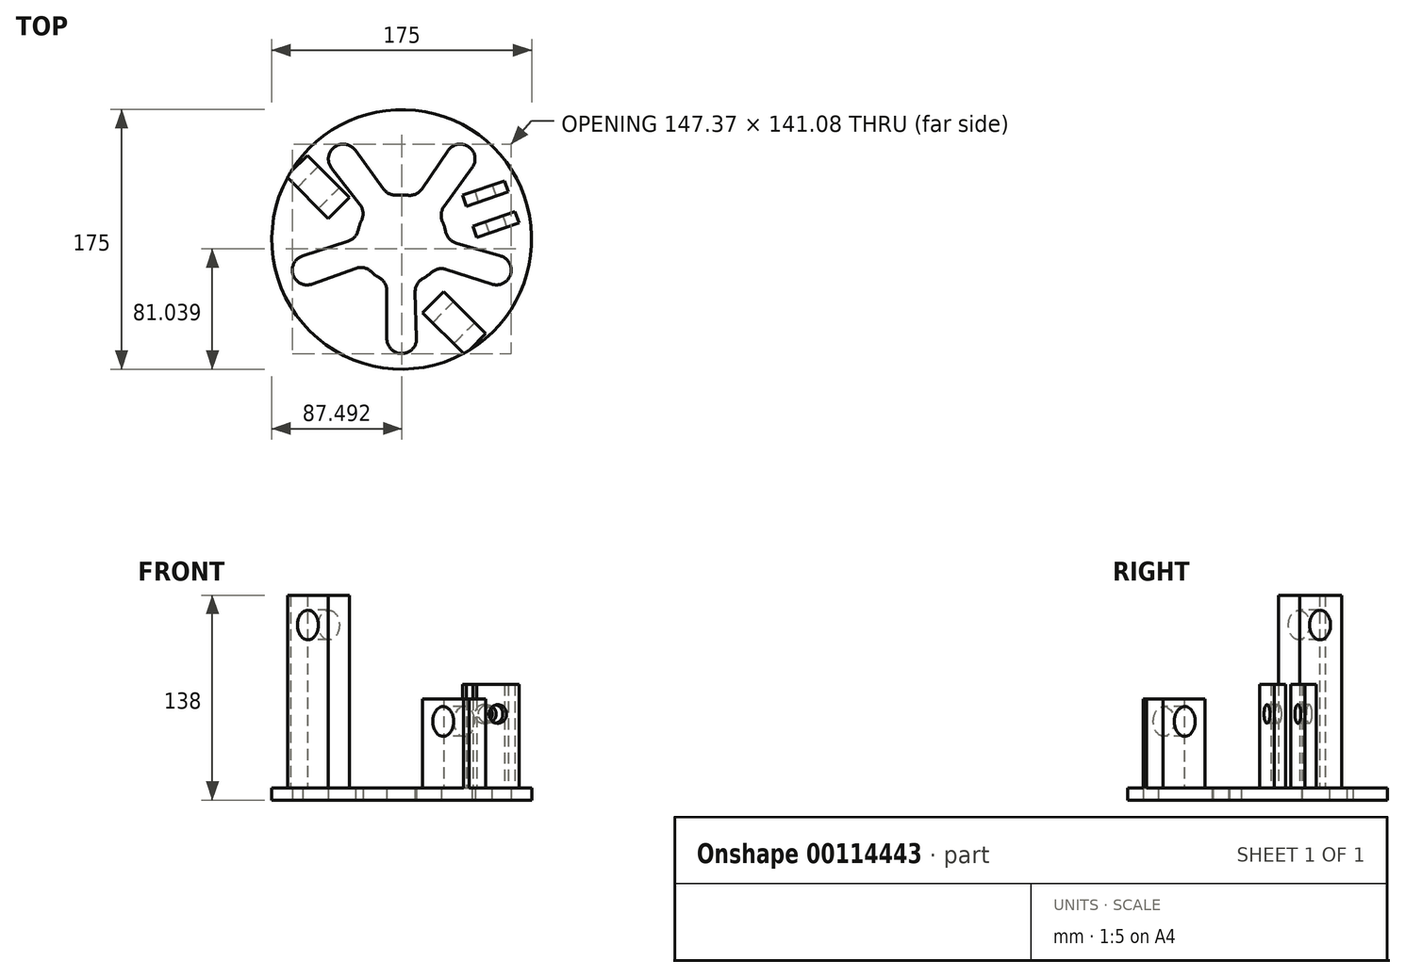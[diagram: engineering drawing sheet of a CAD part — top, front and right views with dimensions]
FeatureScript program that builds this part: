
annotation { "Feature Type Name" : "Feature", "Feature Type Description" : "" }
export const myFeature = defineFeature(function(context is Context, id is Id, definition is map)
    precondition{}
    {
        {
            var Q0;
            Q0=qCreatedBy(makeId("Top.planeOp"),FACE);
            var sketch = newSketch(context, id + "F0", { "sketchPlane" : qUnion([Q0])});
            skCircle(sketch, "E0", {"center": v(0, 0) * mm, "radius": 87.5 * mm});
            skPoint(sketch, "E1.2.0", {"position": v(8.8, -28.68) * mm});
            skLineSegment(sketch, "E1.2.1", {"start": v(-10, -66.87) * mm, "end": v(-10, -34.64) * mm});
            skLineSegment(sketch, "E1.2.2", {"start": v(10, -66.69) * mm, "end": v(9.02, -35.5) * mm});
            skArc(sketch, "E1.2.3", {"start": v(-10, -66.87) * mm, "mid": v(0.1, -77) * mm, "end": v(10, -66.69) * mm});
            skPoint(sketch, "E1.2.4", {"position": v(-10, -28.28) * mm});
            skArc(sketch, "E1.2.5", {"start": v(-10, -34.64) * mm, "mid": v(-11.34, -29.64) * mm, "end": v(-15, -25.98) * mm});
            skArc(sketch, "E1.2.6", {"start": v(14.26, -26.4) * mm, "mid": v(10.35, -30.2) * mm, "end": v(9.02, -35.5) * mm});
            skPoint(sketch, "E2.1.0", {"position": v(30, -0.49) * mm});
            skLineSegment(sketch, "E2.1.1", {"start": v(60.51, -30.17) * mm, "end": v(29.86, -20.21) * mm});
            skLineSegment(sketch, "E2.1.2", {"start": v(66.51, -11.1) * mm, "end": v(36.55, -2.4) * mm});
            skPoint(sketch, "E2.1.3", {"position": v(23.81, -18.25) * mm});
            skArc(sketch, "E2.1.4", {"start": v(60.51, -30.17) * mm, "mid": v(73.26, -23.7) * mm, "end": v(66.51, -11.1) * mm});
            skArc(sketch, "E2.1.5", {"start": v(29.86, -20.21) * mm, "mid": v(24.69, -19.94) * mm, "end": v(20.07, -22.3) * mm});
            skArc(sketch, "E2.1.6", {"start": v(29.5, 5.4) * mm, "mid": v(31.92, 0.5) * mm, "end": v(36.55, -2.4) * mm});
            skPoint(sketch, "E2.2.0", {"position": v(9.73, 28.38) * mm});
            skLineSegment(sketch, "E2.2.1", {"start": v(47.4, 48.22) * mm, "end": v(28.45, 22.15) * mm});
            skLineSegment(sketch, "E2.2.2", {"start": v(31.11, 59.83) * mm, "end": v(13.57, 34.03) * mm});
            skPoint(sketch, "E2.2.3", {"position": v(24.71, 17) * mm});
            skArc(sketch, "E2.2.4", {"start": v(47.4, 48.22) * mm, "mid": v(45.18, 62.35) * mm, "end": v(31.11, 59.83) * mm});
            skArc(sketch, "E2.2.5", {"start": v(28.45, 22.15) * mm, "mid": v(26.6, 17.32) * mm, "end": v(27.4, 12.2) * mm});
            skArc(sketch, "E2.2.6", {"start": v(3.98, 29.74) * mm, "mid": v(9.38, 30.52) * mm, "end": v(13.57, 34.03) * mm});
            skPoint(sketch, "E2.3.0", {"position": v(-23.98, 18.03) * mm});
            skLineSegment(sketch, "E2.3.1", {"start": v(-31.22, 59.98) * mm, "end": v(-12.27, 33.9) * mm});
            skLineSegment(sketch, "E2.3.2", {"start": v(-47.28, 48.08) * mm, "end": v(-28.17, 23.42) * mm});
            skPoint(sketch, "E2.3.3", {"position": v(-8.54, 28.76) * mm});
            skArc(sketch, "E2.3.4", {"start": v(-31.22, 59.98) * mm, "mid": v(-45.33, 62.24) * mm, "end": v(-47.28, 48.08) * mm});
            skArc(sketch, "E2.3.5", {"start": v(-12.27, 33.9) * mm, "mid": v(-8.25, 30.65) * mm, "end": v(-3.14, 29.84) * mm});
            skArc(sketch, "E2.3.6", {"start": v(-27.05, 12.97) * mm, "mid": v(-26.12, 18.36) * mm, "end": v(-28.17, 23.42) * mm});
            skPoint(sketch, "E2.4.0", {"position": v(-24.55, -17.24) * mm});
            skLineSegment(sketch, "E2.4.1", {"start": v(-66.69, -11.16) * mm, "end": v(-36.04, -1.2) * mm});
            skLineSegment(sketch, "E2.4.2", {"start": v(-60.33, -30.11) * mm, "end": v(-30.98, -19.55) * mm});
            skPoint(sketch, "E2.4.3", {"position": v(-30, 0.77) * mm});
            skArc(sketch, "E2.4.4", {"start": v(-66.69, -11.16) * mm, "mid": v(-73.2, -23.88) * mm, "end": v(-60.33, -30.11) * mm});
            skArc(sketch, "E2.4.5", {"start": v(-36.04, -1.2) * mm, "mid": v(-31.7, 1.62) * mm, "end": v(-29.34, 6.24) * mm});
            skArc(sketch, "E2.4.6", {"start": v(-20.7, -21.72) * mm, "mid": v(-25.53, -19.17) * mm, "end": v(-30.98, -19.55) * mm});
            skArc(sketch, "E3", {"start": v(14.26, -26.4) * mm, "mid": v(17.29, -24.52) * mm, "end": v(20.07, -22.3) * mm});
            skArc(sketch, "E4.trimOffspring", {"start": v(29.5, 5.4) * mm, "mid": v(28.66, 8.87) * mm, "end": v(27.4, 12.2) * mm});
            skArc(sketch, "E5.trimOffspring", {"start": v(3.98, 29.74) * mm, "mid": v(0.42, 30) * mm, "end": v(-3.14, 29.84) * mm});
            skArc(sketch, "E6.trimOffspring", {"start": v(-27.05, 12.97) * mm, "mid": v(-28.4, 9.67) * mm, "end": v(-29.34, 6.24) * mm});
            skArc(sketch, "E7.trimOffspring", {"start": v(-20.7, -21.72) * mm, "mid": v(-17.97, -24.02) * mm, "end": v(-15, -25.98) * mm});
            skSolve(sketch);
        }
        {
            var Q0;
            Q0=qSketchRegion(id+"F0",true);
            extrude(context, id + "F1", {"entities" : qUnion([Q0]), "depth" : 8 * mm});
        }
        {
            var Q0;
            Q0=makeQuery(id+"F1.opExtrude","CAP_FACE",FACE,{"disambiguationData":[OSD([sQuery(id+"F0.wireOp",EDGE,"E0"),sQuery(id+"F0.wireOp",EDGE,"CVhEJYwi-Otlj-ANVz-xA45-xXk73iTl9pdf"),sQuery(id+"F0.wireOp",EDGE,"Rns3l94s-3TeN-Ks70-Az69-KKYsNOnhI7OR"),sQuery(id+"F0.wireOp",EDGE,"9CuNRHrq-9yvQ-PRke-7Anj-MRn50c93w0x2"),sQuery(id+"F0.wireOp",EDGE,"WkjIfK7x-7gmP-fVD7-VxIO-WSHESOYnjXVA"),sQuery(id+"F0.wireOp",EDGE,"3d71bf33-8b67-4218-981a-b4396726247d.filletArc"),sQuery(id+"F0.wireOp",EDGE,"c921e2e6-0810-4c6f-9041-cadc7a1e48ec.filletArc"),sQuery(id+"F0.wireOp",EDGE,"E1.1.1"),sQuery(id+"F0.wireOp",EDGE,"E1.1.2"),sQuery(id+"F0.wireOp",EDGE,"E1.1.3"),sQuery(id+"F0.wireOp",EDGE,"E1.1.5"),sQuery(id+"F0.wireOp",EDGE,"E1.1.6"),sQuery(id+"F0.wireOp",EDGE,"E1.2.1"),sQuery(id+"F0.wireOp",EDGE,"E1.2.2"),sQuery(id+"F0.wireOp",EDGE,"E1.2.3"),sQuery(id+"F0.wireOp",EDGE,"E1.2.5"),sQuery(id+"F0.wireOp",EDGE,"E1.2.6"),sQuery(id+"F0.wireOp",EDGE,"E1.3.1"),sQuery(id+"F0.wireOp",EDGE,"E1.3.2"),sQuery(id+"F0.wireOp",EDGE,"E1.3.3"),sQuery(id+"F0.wireOp",EDGE,"E1.3.5"),sQuery(id+"F0.wireOp",EDGE,"E1.3.6"),sQuery(id+"F0.wireOp",EDGE,"f0979199-f49a-472e-a8f6-727d95e7512a.trimOffspring"),sQuery(id+"F0.wireOp",EDGE,"d76e8cd9-870a-43b8-a51b-05d99673c6aa.trimOffspring"),sQuery(id+"F0.wireOp",EDGE,"f797ea8f-0736-4b0c-ab74-ca74c0031448.trimOffspring")])],"isStart":false});
            var sketch = newSketch(context, id + "F2", { "sketchPlane" : qUnion([Q0])});
            skLineSegment(sketch, "E8", {"start": v(121.36, -142.57) * mm, "end": v(-156.99, 135.77) * mm});
            skPoint(sketch, "E9.orphan", {"position": v(-10.6, -10.6) * mm});
            skLineSegment(sketch, "E10", {"start": v(-63.64, 56.57) * mm, "end": v(-35.36, 28.28) * mm});
            skLineSegment(sketch, "E11", {"start": v(-35.36, 28.28) * mm, "end": v(-49.5, 14.14) * mm});
            skLineSegment(sketch, "E12", {"start": v(-49.5, 14.14) * mm, "end": v(-77.78, 42.43) * mm});
            skLineSegment(sketch, "E13", {"start": v(-77.78, 42.43) * mm, "end": v(-63.64, 56.57) * mm});
            skLineSegment(sketch, "E14", {"start": v(65.75, 65.75) * mm, "end": v(-96.48, -96.48) * mm});
            skLineSegment(sketch, "E15.MirrorCS", {"start": v(42.43, -77.78) * mm, "end": v(56.57, -63.64) * mm});
            skLineSegment(sketch, "E16.MirrorCS", {"start": v(14.14, -49.5) * mm, "end": v(42.43, -77.78) * mm});
            skLineSegment(sketch, "E17.MirrorCS", {"start": v(56.57, -63.64) * mm, "end": v(28.28, -35.36) * mm});
            skLineSegment(sketch, "E18.MirrorCS", {"start": v(28.28, -35.36) * mm, "end": v(14.14, -49.5) * mm});
            skSolve(sketch);
        }
        {
            var Q0;
            {var subQ5=sQuery(id+"F2.wireOp",EDGE,"E8");var subQ7=sQuery(id+"F2.wireOp",EDGE,"E15.MirrorCS");var subQ8=makeQuery(id+"F2.imprint","INTERSECT",VERTEX,{"derivedFrom":[subQ5,subQ7]});Q0=makeQuery(id+"F2.imprint","IMPRINT",FACE,{"disambiguationData":[TD([[makeQuery(id+"F2.imprint","IMPRINT",EDGE,{"disambiguationData":[TD([[subQ8,-1.0]])],"derivedFrom":subQ5}),1.0]])]});}
            var Q1;
            {var subQ5=sQuery(id+"F2.wireOp",EDGE,"E17.MirrorCS");Q1=makeQuery(id+"F2.imprint","IMPRINT",FACE,{"disambiguationData":[TD([[makeQuery(id+"F2.imprint","IMPRINT",EDGE,{"derivedFrom":subQ5}),1.0]])]});}
            extrude(context, id + "F3", {"entities" : qUnion([Q0, Q1]), "operationType" : NewBodyOperationType.ADD, "depth" : 60 * mm});
        }
        {
            var Q0;
            {var subQ1=sQuery(id+"F2.wireOp",EDGE,"E11");var subQ5=sQuery(id+"F2.wireOp",EDGE,"E8");var subQ6=makeQuery(id+"F2.imprint","INTERSECT",VERTEX,{"derivedFrom":[subQ5,subQ1]});Q0=makeQuery(id+"F2.imprint","IMPRINT",FACE,{"disambiguationData":[TD([[makeQuery(id+"F2.imprint","IMPRINT",EDGE,{"disambiguationData":[TD([[subQ6,-1.0]])],"derivedFrom":subQ5}),1.0]])]});}
            var Q1;
            {var subQ5=sQuery(id+"F2.wireOp",EDGE,"E10");Q1=makeQuery(id+"F2.imprint","IMPRINT",FACE,{"disambiguationData":[TD([[makeQuery(id+"F2.imprint","IMPRINT",EDGE,{"derivedFrom":subQ5}),-1.0]])]});}
            extrude(context, id + "F4", {"entities" : qUnion([Q0, Q1]), "operationType" : NewBodyOperationType.ADD, "depth" : 130 * mm});
        }
        {
            var Q0;
            Q0=makeQuery(id+"F4.opExtrude","SWEPT_FACE",FACE,{"disambiguationData":[OSD([sQuery(id+"F2.wireOp",EDGE,"E12")])]});
            var sketch = newSketch(context, id + "F5", { "sketchPlane" : qUnion([Q0])});
            skCircle(sketch, "E19", {"center": v(-64.43, 118) * mm, "radius": 10 * mm});
            skPoint(sketch, "E19.centerSnap0", {"position": v(-64.43, 138) * mm});
            skSolve(sketch);
        }
        {
            var Q0;
            Q0=qSketchRegion(id+"F5",true);
            extrude(context, id + "F6", {"entities" : qUnion([Q0]), "operationType" : NewBodyOperationType.REMOVE, "endBound" : BoundingType.THROUGH_ALL, "oppositeDirection" : true, "depth" : 25 * mm});
        }
        {
            var Q0;
            Q0=makeQuery(id+"F3.opExtrude","SWEPT_FACE",FACE,{"disambiguationData":[OSD([sQuery(id+"F2.wireOp",EDGE,"E16.MirrorCS")])]});
            var sketch = newSketch(context, id + "F7", { "sketchPlane" : qUnion([Q0])});
            skCircle(sketch, "E20", {"center": v(64.43, 53) * mm, "radius": 10 * mm});
            skPoint(sketch, "E20.centerSnap0", {"position": v(64.43, 68) * mm});
            skSolve(sketch);
        }
        {
            var Q0;
            Q0=makeQuery(id+"F7.imprint","IMPRINT",FACE,{"disambiguationData":[TD([[makeQuery(id+"F7.imprint","IMPRINT",EDGE,{"derivedFrom":sQuery(id+"F7.wireOp",EDGE,"E20")}),1.0]])]});
            extrude(context, id + "F8", {"entities" : qUnion([Q0]), "operationType" : NewBodyOperationType.REMOVE, "endBound" : BoundingType.THROUGH_ALL, "oppositeDirection" : true, "depth" : 25 * mm});
        }
        {
            var Q0;
            Q0=qCreatedBy(makeId("Top.planeOp"),FACE);
            var sketch = newSketch(context, id + "F9", { "sketchPlane" : qUnion([Q0])});
            skArc(sketch, "E21.0", {"start": v(65.88, -57.59) * mm, "mid": v(83.28, 26.84) * mm, "end": v(19.84, 85.22) * mm});
            skArc(sketch, "E22.0", {"start": v(3.98, 29.74) * mm, "mid": v(9.38, 30.52) * mm, "end": v(13.57, 34.03) * mm});
            skLineSegment(sketch, "E23.0", {"start": v(31.11, 59.83) * mm, "end": v(13.57, 34.03) * mm});
            skArc(sketch, "E24.0", {"start": v(47.4, 48.22) * mm, "mid": v(45.18, 62.35) * mm, "end": v(31.11, 59.83) * mm});
            skLineSegment(sketch, "E25.0", {"start": v(47.4, 48.22) * mm, "end": v(28.45, 22.15) * mm});
            skArc(sketch, "E26.0", {"start": v(28.45, 22.15) * mm, "mid": v(26.6, 17.32) * mm, "end": v(27.4, 12.2) * mm});
            skArc(sketch, "E27.0", {"start": v(29.5, 5.4) * mm, "mid": v(28.66, 8.87) * mm, "end": v(27.4, 12.2) * mm});
            skArc(sketch, "E28.0", {"start": v(29.5, 5.4) * mm, "mid": v(31.92, 0.5) * mm, "end": v(36.55, -2.4) * mm});
            skLineSegment(sketch, "E29.0", {"start": v(66.51, -11.1) * mm, "end": v(36.55, -2.4) * mm});
            skArc(sketch, "E30.0", {"start": v(60.51, -30.17) * mm, "mid": v(73.26, -23.7) * mm, "end": v(66.51, -11.1) * mm});
            skLineSegment(sketch, "E31.0", {"start": v(60.51, -30.17) * mm, "end": v(29.86, -20.21) * mm});
            skArc(sketch, "E32.0", {"start": v(29.86, -20.21) * mm, "mid": v(24.69, -19.94) * mm, "end": v(20.07, -22.3) * mm});
            skArc(sketch, "E33.0", {"start": v(3.98, 29.74) * mm, "mid": v(2, 29.93) * mm, "end": v(0, 30) * mm});
            skLineSegment(sketch, "E34", {"start": v(18.86, -35.85) * mm, "end": v(35.02, -56.68) * mm});
            skPoint(sketch, "E35.orphan", {"position": v(-3.14, 29.84) * mm});
            skPoint(sketch, "E36.orphan", {"position": v(14.26, -26.4) * mm});
            skPoint(sketch, "E37.orphan", {"position": v(-74.79, 45.42) * mm});
            skPoint(sketch, "E38.orphan", {"position": v(45.42, -74.79) * mm});
            skPoint(sketch, "E39.visualSharp", {"position": v(0, 87.5) * mm});
            skArc(sketch, "E40.filletArc", {"start": v(35.02, -56.68) * mm, "mid": v(50.23, -64.42) * mm, "end": v(65.88, -57.59) * mm});
            skArc(sketch, "E41", {"start": v(-4.7, 40) * mm, "mid": v(2.2, 30.14) * mm, "end": v(13.57, 34.03) * mm});
            skArc(sketch, "E42", {"start": v(29.86, -20.21) * mm, "mid": v(18.58, -23.97) * mm, "end": v(18.86, -35.85) * mm});
            skLineSegment(sketch, "E43", {"start": v(-4.7, 40) * mm, "end": v(-4.7, 65.74) * mm});
            skArc(sketch, "E44.filletArc", {"start": v(19.84, 85.22) * mm, "mid": v(2.87, 81.4) * mm, "end": v(-4.7, 65.74) * mm});
            skSolve(sketch);
        }
        {
            var Q0;
            Q0=makeQuery(id+"F9.imprint","IMPRINT",FACE,{"disambiguationData":[TD([[makeQuery(id+"F9.imprint","IMPRINT",EDGE,{"derivedFrom":sQuery(id+"F9.wireOp",EDGE,"E21.0")}),1.0]])]});
            extrude(context, id + "F10", {"entities" : qUnion([Q0]), "depth" : 8 * mm});
        }
        {
            var Q0;
            Q0=makeQuery(id+"F10.opExtrude","CAP_FACE",FACE,{"disambiguationData":[OSD([sQuery(id+"F9.wireOp",EDGE,"E21.0"),sQuery(id+"F9.wireOp",EDGE,"E23.0"),sQuery(id+"F9.wireOp",EDGE,"E24.0"),sQuery(id+"F9.wireOp",EDGE,"E25.0"),sQuery(id+"F9.wireOp",EDGE,"E26.0"),sQuery(id+"F9.wireOp",EDGE,"E27.0"),sQuery(id+"F9.wireOp",EDGE,"E28.0"),sQuery(id+"F9.wireOp",EDGE,"E29.0"),sQuery(id+"F9.wireOp",EDGE,"E30.0"),sQuery(id+"F9.wireOp",EDGE,"E31.0"),sQuery(id+"F9.wireOp",EDGE,"E34"),sQuery(id+"F9.wireOp",EDGE,"E40.filletArc"),sQuery(id+"F9.wireOp",EDGE,"E41"),sQuery(id+"F9.wireOp",EDGE,"E42"),sQuery(id+"F9.wireOp",EDGE,"E43"),sQuery(id+"F9.wireOp",EDGE,"E44.filletArc")])],"isStart":false});
            var sketch = newSketch(context, id + "F11", { "sketchPlane" : qUnion([Q0])});
            skLineSegment(sketch, "E45", {"start": v(0, 0) * mm, "end": v(93.05, 31.85) * mm});
            skLineSegment(sketch, "E46", {"start": v(43.54, 22.3) * mm, "end": v(71.8, 31.98) * mm});
            skLineSegment(sketch, "E47", {"start": v(71.8, 31.98) * mm, "end": v(69.2, 39.54) * mm});
            skLineSegment(sketch, "E48", {"start": v(69.2, 39.54) * mm, "end": v(40.82, 29.83) * mm});
            skLineSegment(sketch, "E49", {"start": v(40.82, 29.83) * mm, "end": v(43.54, 22.3) * mm});
            skLineSegment(sketch, "E50.MirrorCS", {"start": v(50.54, 1.45) * mm, "end": v(48.07, 9.06) * mm});
            skLineSegment(sketch, "E51.MirrorCS", {"start": v(78.92, 11.16) * mm, "end": v(50.54, 1.45) * mm});
            skLineSegment(sketch, "E52.MirrorCS", {"start": v(48.07, 9.06) * mm, "end": v(76.33, 18.73) * mm});
            skLineSegment(sketch, "E53.MirrorCS", {"start": v(76.33, 18.73) * mm, "end": v(78.92, 11.16) * mm});
            skSolve(sketch);
        }
        {
            var Q0;
            Q0=makeQuery(id+"F11.imprint","IMPRINT",FACE,{"disambiguationData":[TD([[makeQuery(id+"F11.imprint","IMPRINT",EDGE,{"derivedFrom":sQuery(id+"F11.wireOp",EDGE,"E46")}),1.0]])]});
            var Q1;
            Q1=makeQuery(id+"F11.imprint","IMPRINT",FACE,{"disambiguationData":[TD([[makeQuery(id+"F11.imprint","IMPRINT",EDGE,{"derivedFrom":sQuery(id+"F11.wireOp",EDGE,"E50.MirrorCS")}),-1.0]])]});
            extrude(context, id + "F12", {"entities" : qUnion([Q0, Q1]), "operationType" : NewBodyOperationType.ADD, "depth" : 70 * mm});
        }
        {
            var Q0;
            Q0=makeQuery(id+"F12.opExtrude","SWEPT_FACE",FACE,{"disambiguationData":[OSD([sQuery(id+"F11.wireOp",EDGE,"E51.MirrorCS")])]});
            var sketch = newSketch(context, id + "F13", { "sketchPlane" : qUnion([Q0])});
            skCircle(sketch, "E54", {"center": v(63.28, 58) * mm, "radius": 6.25 * mm});
            skPoint(sketch, "E54.centerSnap0", {"position": v(63.28, 78) * mm});
            skSolve(sketch);
        }
        {
            var Q0;
            Q0 = qSketchRegion(id + "F13", true);
            extrude(context, id + "F14", {"entities" : qUnion([Q0]), "operationType" : NewBodyOperationType.REMOVE, "endBound" : BoundingType.THROUGH_ALL, "oppositeDirection" : true, "depth" : 25 * mm});
        }
    });
